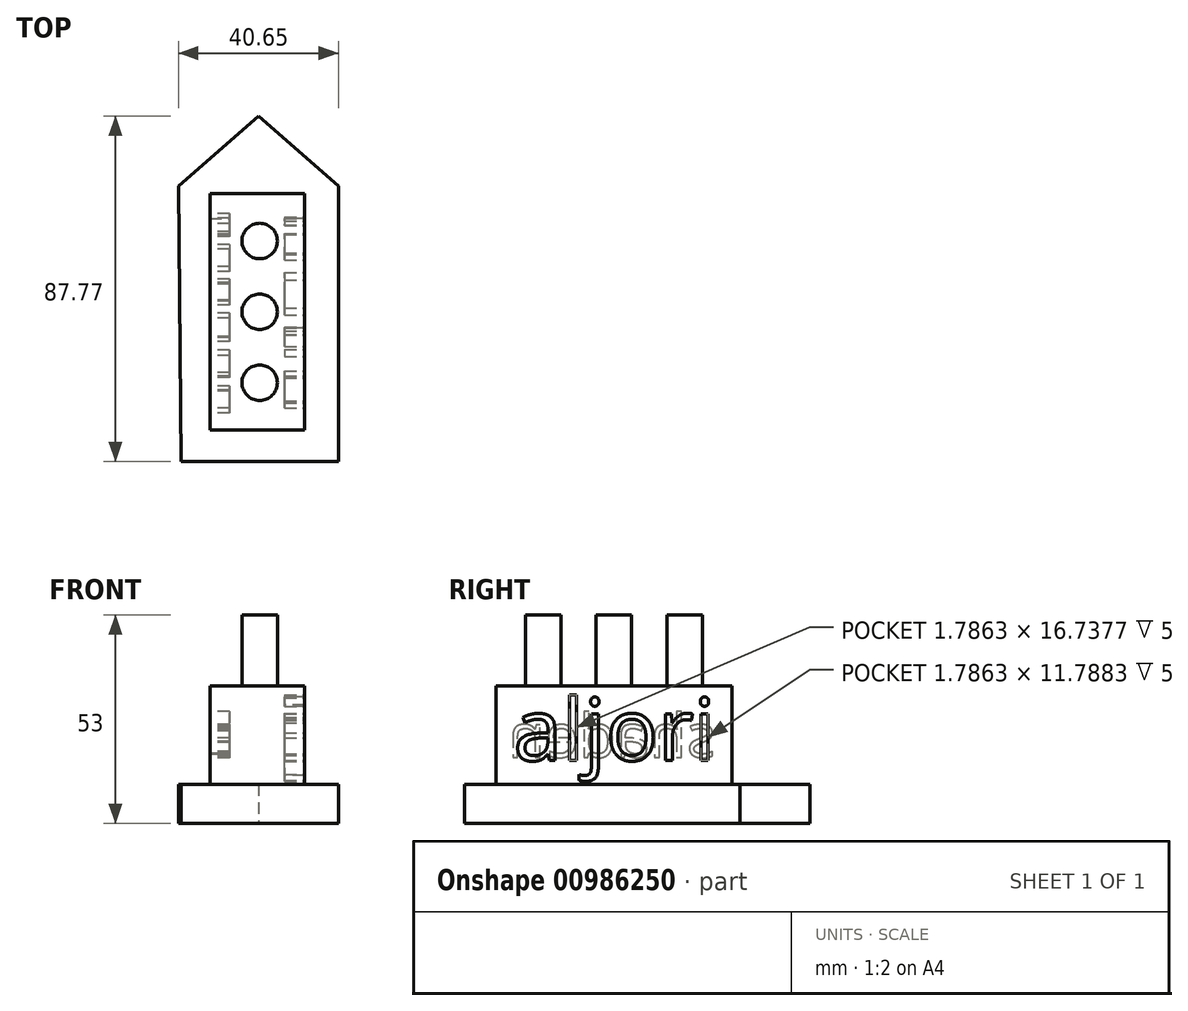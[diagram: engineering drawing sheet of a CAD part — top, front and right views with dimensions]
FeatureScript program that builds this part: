
annotation { "Feature Type Name" : "Feature", "Feature Type Description" : "" }
export const myFeature = defineFeature(function(context is Context, id is Id, definition is map)
    precondition{}
    {
        {
            var Q0;
            Q0=qCreatedBy(makeId("Top.planeOp"),FACE);
            var sketch = newSketch(context, id + "F0", { "sketchPlane" : qUnion([Q0])});
            skLineSegment(sketch, "E0", {"start": v(20, 41.47) * mm, "end": v(20, -28.53) * mm});
            skLineSegment(sketch, "E1", {"start": v(20, -28.53) * mm, "end": v(-20, -28.53) * mm});
            skLineSegment(sketch, "E2", {"start": v(-20.65, 41.47) * mm, "end": v(-20, -28.53) * mm});
            skLineSegment(sketch, "E3", {"start": v(20, 41.47) * mm, "end": v(-0.33, 59.24) * mm});
            skLineSegment(sketch, "E4", {"start": v(-0.33, 59.24) * mm, "end": v(-20.65, 41.47) * mm});
            skSolve(sketch);
        }
        {
            var Q0;
            Q0=makeQuery(id+"F0.imprint","IMPRINT",FACE,{"disambiguationData":[TD([[makeQuery(id+"F0.imprint","IMPRINT",EDGE,{"derivedFrom":sQuery(id+"F0.wireOp",EDGE,"E0")}),-1.0]])]});
            extrude(context, id + "F1", {"entities" : qUnion([Q0]), "depth" : 10 * mm, "offsetDistance" : 25 * mm});
        }
        {
            var Q0;
            Q0=makeQuery(id+"F1.opExtrude","CAP_FACE",FACE,{"disambiguationData":[OSD([sQuery(id+"F0.wireOp",EDGE,"E0"),sQuery(id+"F0.wireOp",EDGE,"E1"),sQuery(id+"F0.wireOp",EDGE,"E2"),sQuery(id+"F0.wireOp",EDGE,"E3"),sQuery(id+"F0.wireOp",EDGE,"E4")])],"isStart":false});
            var sketch = newSketch(context, id + "F2", { "sketchPlane" : qUnion([Q0])});
            skLineSegment(sketch, "E5.bottom", {"start": v(-12.63, 39.47) * mm, "end": v(11.37, 39.47) * mm});
            skLineSegment(sketch, "E5.top", {"start": v(-12.63, -20.53) * mm, "end": v(11.37, -20.53) * mm});
            skLineSegment(sketch, "E5.left", {"start": v(-12.63, 39.47) * mm, "end": v(-12.63, -20.53) * mm});
            skLineSegment(sketch, "E5.right", {"start": v(11.37, 39.47) * mm, "end": v(11.37, -20.53) * mm});
            skSolve(sketch);
        }
        {
            var Q0;
            Q0 = qSketchRegion(id + "F2", true);
            extrude(context, id + "F3", {"entities" : qUnion([Q0]), "operationType" : NewBodyOperationType.ADD, "depth" : 25 * mm, "offsetDistance" : 25 * mm});
        }
        {
            var Q0;
            Q0=makeQuery(id+"F3.opExtrude","CAP_FACE",FACE,{"disambiguationData":[OSD([sQuery(id+"F2.wireOp",EDGE,"E5.bottom"),sQuery(id+"F2.wireOp",EDGE,"E5.top"),sQuery(id+"F2.wireOp",EDGE,"E5.left"),sQuery(id+"F2.wireOp",EDGE,"E5.right")])],"isStart":false});
            var sketch = newSketch(context, id + "F4", { "sketchPlane" : qUnion([Q0])});
            skCircle(sketch, "E6", {"center": v(0, 27.47) * mm, "radius": 4.5 * mm});
            skCircle(sketch, "E7", {"center": v(0, 9.47) * mm, "radius": 4.5 * mm});
            skCircle(sketch, "E8", {"center": v(0, -8.53) * mm, "radius": 4.5 * mm});
            skSolve(sketch);
        }
        {
            var Q0;
            Q0 = qSketchRegion(id + "F4", true);
            extrude(context, id + "F5", {"entities" : qUnion([Q0]), "operationType" : NewBodyOperationType.ADD, "depth" : 18 * mm, "offsetDistance" : 25 * mm});
        }
        {
            var Q0;
            Q0=makeQuery(id+"F3.opExtrude","SWEPT_FACE",FACE,{"disambiguationData":[OSD([sQuery(id+"F2.wireOp",EDGE,"E5.right")])]});
            var sketch = newSketch(context, id + "F6", { "sketchPlane" : qUnion([Q0])});
            skText(sketch, "E9", { "text": "aljori", "fontName": "OpenSans-Regular.ttf"});
            const initialGuessF6  = {"E9": [-0.016, 0.016, 1, 0, 0.01586]};
            skSetInitialGuess(sketch, initialGuessF6);
            skSolve(sketch);
        }
        {
            var Q0;
            Q0 = qSketchRegion(id + "F6", true);
            extrude(context, id + "F7", {"entities" : qUnion([Q0]), "operationType" : NewBodyOperationType.REMOVE, "oppositeDirection" : true, "depth" : 5 * mm, "offsetDistance" : 25 * mm});
        }
        {
            var Q0;
            Q0=makeQuery(id+"F3.opExtrude","SWEPT_FACE",FACE,{"disambiguationData":[OSD([sQuery(id+"F2.wireOp",EDGE,"E5.left")])]});
            var sketch = newSketch(context, id + "F8", { "sketchPlane" : qUnion([Q0])});
            skText(sketch, "E10", { "text": "shaden", "fontName": "OpenSans-Regular.ttf"});
            const initialGuessF8  = {"E10": [-0.03527, 0.01685, 1, 0, 0.01105]};
            skSetInitialGuess(sketch, initialGuessF8);
            skSolve(sketch);
        }
        {
            var Q0;
            Q0 = qSketchRegion(id + "F8", true);
            extrude(context, id + "F9", {"entities" : qUnion([Q0]), "operationType" : NewBodyOperationType.REMOVE, "oppositeDirection" : true, "depth" : 5 * mm, "offsetDistance" : 25 * mm});
        }
    });
